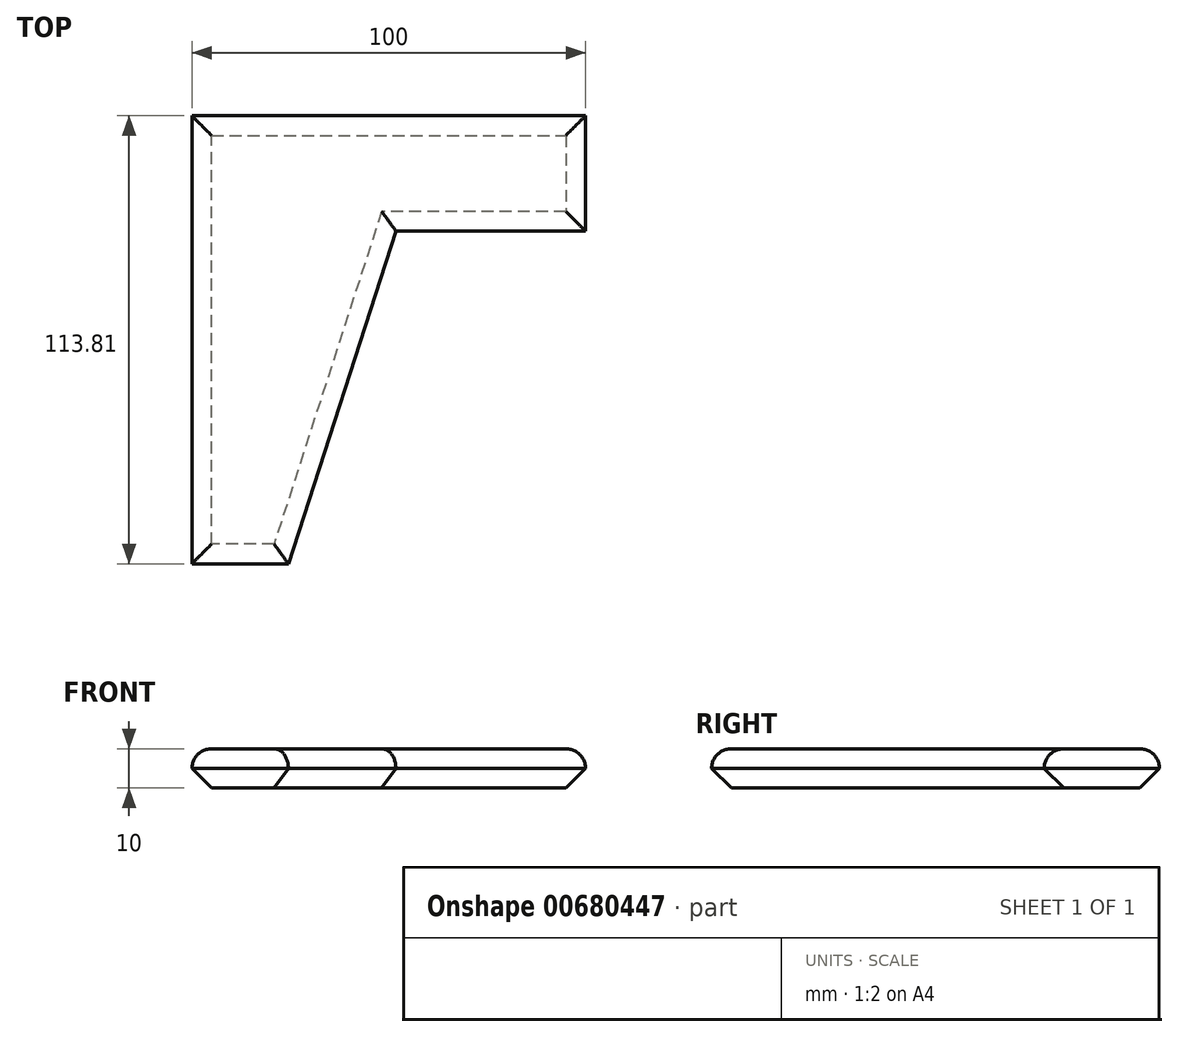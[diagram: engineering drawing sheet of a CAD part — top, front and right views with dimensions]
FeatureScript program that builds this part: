
annotation { "Feature Type Name" : "Feature", "Feature Type Description" : "" }
export const myFeature = defineFeature(function(context is Context, id is Id, definition is map)
    precondition{}
    {
        {
            var Q0;
            Q0=qCreatedBy(makeId("Top.planeOp"),FACE);
            var sketch = newSketch(context, id + "F0", { "sketchPlane" : qUnion([Q0])});
            skLineSegment(sketch, "E0", {"start": v(-57.75, 60.78) * mm, "end": v(42.25, 60.78) * mm});
            skLineSegment(sketch, "E1", {"start": v(42.25, 60.78) * mm, "end": v(42.25, 31.48) * mm});
            skLineSegment(sketch, "E2", {"start": v(42.25, 31.48) * mm, "end": v(-5.92, 31.48) * mm});
            skLineSegment(sketch, "E3", {"start": v(-5.92, 31.48) * mm, "end": v(-33.24, -53.03) * mm});
            skLineSegment(sketch, "E4", {"start": v(-33.24, -53.03) * mm, "end": v(-57.75, -53.03) * mm});
            skLineSegment(sketch, "E5", {"start": v(-57.75, -53.03) * mm, "end": v(-57.75, 60.78) * mm});
            skSolve(sketch);
        }
        {
            var Q0;
            Q0 = qSketchRegion(id + "F0", true);
            extrude(context, id + "F1", {"entities" : qUnion([Q0]), "depth" : 10 * mm, "offsetDistance" : 25 * mm});
        }
        {
            var Q0;
            Q0=makeQuery(id+"F1.opExtrude","CAP_EDGE",EDGE,{"disambiguationData":[OSD([sQuery(id+"F0.wireOp",EDGE,"E5")])],"isStart":false});
            var Q1;
            Q1=makeQuery(id+"F1.opExtrude","CAP_EDGE",EDGE,{"disambiguationData":[OSD([sQuery(id+"F0.wireOp",EDGE,"E3")])],"isStart":false});
            var Q2;
            Q2=makeQuery(id+"F1.opExtrude","CAP_EDGE",EDGE,{"disambiguationData":[OSD([sQuery(id+"F0.wireOp",EDGE,"E4")])],"isStart":false});
            var Q3;
            Q3=makeQuery(id+"F1.opExtrude","CAP_EDGE",EDGE,{"disambiguationData":[OSD([sQuery(id+"F0.wireOp",EDGE,"E2")])],"isStart":false});
            var Q4;
            Q4=makeQuery(id+"F1.opExtrude","CAP_EDGE",EDGE,{"disambiguationData":[OSD([sQuery(id+"F0.wireOp",EDGE,"E0")])],"isStart":false});
            var Q5;
            Q5=makeQuery(id+"F1.opExtrude","CAP_EDGE",EDGE,{"disambiguationData":[OSD([sQuery(id+"F0.wireOp",EDGE,"E1")])],"isStart":false});
            fillet(context, id + "F2", {"entities" : qUnion([Q0, Q1, Q2, Q3, Q4, Q5]), "radius" : 5 * mm, "tangentPropagation" : true, "allowEdgeOverflow" : false});
        }
        {
            var Q0;
            Q0=makeQuery(id+"F1.opExtrude","CAP_FACE",FACE,{"disambiguationData":[OSD([sQuery(id+"F0.wireOp",EDGE,"E0"),sQuery(id+"F0.wireOp",EDGE,"E1"),sQuery(id+"F0.wireOp",EDGE,"E2"),sQuery(id+"F0.wireOp",EDGE,"E3"),sQuery(id+"F0.wireOp",EDGE,"E4"),sQuery(id+"F0.wireOp",EDGE,"E5")])],"isStart":true});
            chamfer(context, id + "F3", {"entities" : qUnion([Q0]), "width" : 5 * mm, "tangentPropagation" : true});
        }
    });
